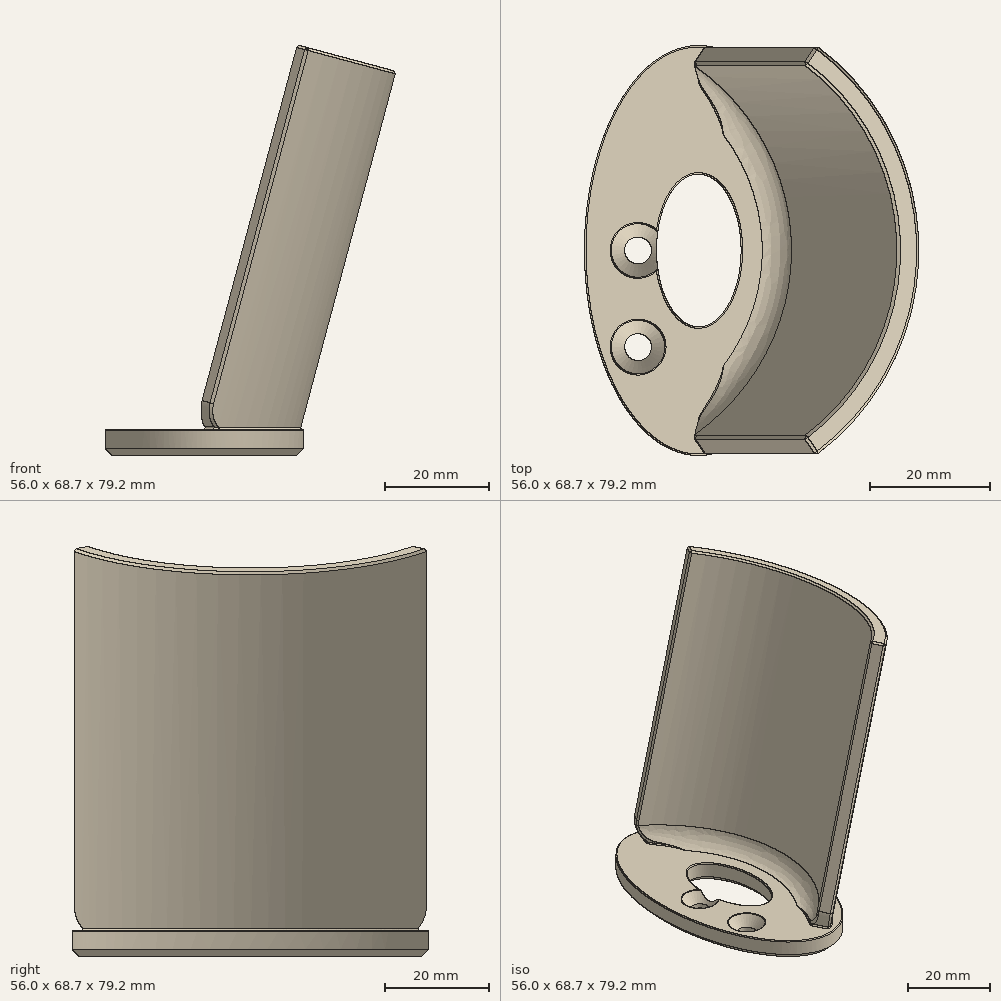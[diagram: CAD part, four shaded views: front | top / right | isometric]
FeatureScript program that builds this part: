
annotation { "Feature Type Name" : "Feature", "Feature Type Description" : "" }
export const myFeature = defineFeature(function(context is Context, id is Id, definition is map)
    precondition{}
    {
        {
            var Q0;
            Q0=qCreatedBy(makeId("Top.planeOp"),FACE);
            var sketch = newSketch(context, id + "F0", { "sketchPlane" : qUnion([Q0])});
            skLineSegment(sketch, "E0", {"start": v(0, -32.6) * mm, "end": v(0, 55.82) * mm, "construction": true});
            skSolve(sketch);
        }
        {
            var Q0;
            Q0=sQuery(id+"F0.wireOp",EDGE,"E0");
            cPlane(context, id + "F1", {"entities" : qUnion([Q0]), "cplaneType" : CPlaneType.LINE_ANGLE, "offset" : 25.4 * mm, "angle" : 15 * degree, "width" : 152.4 * mm, "height" : 152.4 * mm});
        }
        {
            var Q0;
            Q0=qCreatedBy(id+"F1.planeOp",FACE);
            var sketch = newSketch(context, id + "F2", { "sketchPlane" : qUnion([Q0])});
            skArc(sketch, "E1", {"start": v(21.85, -31.2) * mm, "mid": v(38.1, 0) * mm, "end": v(21.85, 31.2) * mm});
            skArc(sketch, "E2", {"start": v(24.04, -34.33) * mm, "mid": v(41.91, 0) * mm, "end": v(24.04, 34.33) * mm});
            skLineSegment(sketch, "E3", {"start": v(21.85, -31.2) * mm, "end": v(24.04, -34.33) * mm});
            skLineSegment(sketch, "E4", {"start": v(-21.31, 0) * mm, "end": v(0, 0) * mm, "construction": true});
            skLineSegment(sketch, "E5.MirrorCS", {"start": v(21.85, 31.2) * mm, "end": v(24.04, 34.33) * mm});
            skPoint(sketch, "E6.orphan", {"position": v(31.22, -44.6) * mm});
            skPoint(sketch, "E7.orphan", {"position": v(31.22, 44.6) * mm});
            skSolve(sketch);
        }
        {
            var Q0;
            Q0 = qSketchRegion(id + "F2", true);
            extrude(context, id + "F3", {"entities" : qUnion([Q0]), "depth" : 76.2 * mm});
        }
        {
            var Q0;
            Q0=qCreatedBy(makeId("Top.planeOp"),FACE);
            cPlane(context, id + "F4", {"entities" : qUnion([Q0]), "cplaneType" : CPlaneType.OFFSET, "offset" : 6.35 * mm, "oppositeDirection" : true, "width" : 152.4 * mm, "height" : 152.4 * mm});
        }
        {
            var Q0;
            Q0=qCreatedBy(id+"F4.planeOp",FACE);
            var sketch = newSketch(context, id + "F5", { "sketchPlane" : qUnion([Q0])});
            skLineSegment(sketch, "E8", {"start": v(23.22, 34.33) * mm, "end": v(23.22, -44.52) * mm, "construction": true});
            skEllipse(sketch, "E9", {"center": v(23.22, 0) * mm, "majorRadius": 34.33 * mm, "minorRadius": 19.16 * mm, "majorAxis": v(0, 1)});
            skSolve(sketch);
        }
        {
            var Q0;
            Q0 = qSketchRegion(id + "F5", true);
            extrude(context, id + "F6", {"entities" : qUnion([Q0]), "operationType" : NewBodyOperationType.ADD, "oppositeDirection" : true, "depth" : 5.08 * mm});
        }
        {
            var Q0;
            Q0=makeQuery(id+"F6.opExtrude","CAP_FACE",FACE,{"disambiguationData":[OSD([sQuery(id+"F5.wireOp",EDGE,"E9")])],"isStart":true});
            var sketch = newSketch(context, id + "F7", { "sketchPlane" : qUnion([Q0])});
            skEllipse(sketch, "E10", {"center": v(23.22, 0) * mm, "majorRadius": 12.78 * mm, "minorRadius": 7.1 * mm, "majorAxis": v(0, 1)});
            skSolve(sketch);
        }
        {
            var Q0;
            Q0 = qSketchRegion(id + "F7", true);
            extrude(context, id + "F8", {"entities" : qUnion([Q0]), "operationType" : NewBodyOperationType.REMOVE, "oppositeDirection" : true, "depth" : 25.4 * mm});
        }
        {
            var Q0;
            Q0=makeQuery(id+"F6.opExtrude","CAP_FACE",FACE,{"disambiguationData":[OSD([sQuery(id+"F5.wireOp",EDGE,"E9")])],"isStart":true});
            var sketch = newSketch(context, id + "F9", { "sketchPlane" : qUnion([Q0])});
            skLineSegment(sketch, "E11", {"start": v(13.06, -34.14) * mm, "end": v(13.06, 47.46) * mm, "construction": true});
            skPoint(sketch, "E12", {"position": v(13.06, -16.19) * mm});
            skLineSegment(sketch, "E13", {"start": v(23.22, 0) * mm, "end": v(23.22, -16.19) * mm, "construction": true});
            skPoint(sketch, "E14", {"position": v(13.06, 0) * mm});
            skSolve(sketch);
        }
        {
            var Q0;
            Q0=sQuery(id+"F9.wireOp",VERTEX,"E12");
            var Q1;
            Q1=makeQuery(id+"F3.opExtrude","SWEPT_BODY",BODY,{"disambiguationData":[OSD([sQuery(id+"F2.wireOp",EDGE,"E1"),sQuery(id+"F2.wireOp",EDGE,"E2"),sQuery(id+"F2.wireOp",EDGE,"E3"),sQuery(id+"F2.wireOp",EDGE,"E5.MirrorCS")])]});
            hole(context, id + "F10", {"style" : HoleStyle.C_SINK, "endStyle" : HoleEndStyle.BLIND, "standardTappedOrClearance" : lookupTablePath({ "standard" : "ANSI", "fit" : "Normal (ASME)", "size" : "#8", "type" : "Clearance" }), "standardBlindInLast" : lookupTablePath({ "fit" : "Free", "standard" : "ANSI", "size" : "#8", "type" : "Clearance" }), "holeDiameter" : 4.5 * mm, "cSinkDiameter" : 9.12 * mm, "cSinkAngle" : 82 * degree, "holeDepth" : 12.7 * mm, "isTappedThrough" : true, "tappedDepth" : 12.7 * mm, "tapClearance" : 3, "locations" : qUnion([Q0]), "scope" : qUnion([Q1])});
        }
        {
            var Q0;
            Q0=sQuery(id+"F9.wireOp",VERTEX,"E14");
            var Q1;
            Q1=makeQuery(id+"F3.opExtrude","SWEPT_BODY",BODY,{"disambiguationData":[OSD([sQuery(id+"F2.wireOp",EDGE,"E1"),sQuery(id+"F2.wireOp",EDGE,"E2"),sQuery(id+"F2.wireOp",EDGE,"E3"),sQuery(id+"F2.wireOp",EDGE,"E5.MirrorCS")])]});
            hole(context, id + "F11", {"style" : HoleStyle.C_SINK, "endStyle" : HoleEndStyle.BLIND, "standardTappedOrClearance" : lookupTablePath({ "standard" : "ANSI", "fit" : "Normal (ASME)", "size" : "#8", "type" : "Clearance" }), "standardBlindInLast" : lookupTablePath({ "fit" : "Free", "standard" : "ANSI", "size" : "#8", "type" : "Clearance" }), "holeDiameter" : 4.5 * mm, "cSinkDiameter" : 9.12 * mm, "cSinkAngle" : 82 * degree, "holeDepth" : 12.7 * mm, "isTappedThrough" : true, "tappedDepth" : 12.7 * mm, "tapClearance" : 3, "locations" : qUnion([Q0]), "scope" : qUnion([Q1])});
        }
        {
            var Q0;
            Q0=makeQuery(id+"F6.boolean.opBoolean","INTERSECT",EDGE,{"derivedFrom":[makeQuery(id+"F3.opExtrude","SWEPT_FACE",FACE,{"disambiguationData":[OSD([sQuery(id+"F2.wireOp",EDGE,"E1")])]}),makeQuery(id+"F6.opExtrude","CAP_FACE",FACE,{"disambiguationData":[OSD([sQuery(id+"F5.wireOp",EDGE,"E9")])],"isStart":true})]});
            fillet(context, id + "F12", {"entities" : qUnion([Q0]), "radius" : 5.08 * mm, "tangentPropagation" : true, "allowEdgeOverflow" : false});
        }
        {
            var Q0;
            Q0=makeQuery(id+"F3.opExtrude","CAP_EDGE",EDGE,{"disambiguationData":[OSD([sQuery(id+"F2.wireOp",EDGE,"E3")])],"isStart":true});
            var Q1;
            Q1=makeQuery(id+"F3.opExtrude","CAP_EDGE",EDGE,{"disambiguationData":[OSD([sQuery(id+"F2.wireOp",EDGE,"E5.MirrorCS")])],"isStart":true});
            fillet(context, id + "F13", {"entities" : qUnion([Q0, Q1]), "radius" : 5.08 * mm, "tangentPropagation" : true, "allowEdgeOverflow" : false});
        }
        {
            var Q0;
            Q0=makeQuery(id+"F6.opExtrude","CAP_FACE",FACE,{"disambiguationData":[OSD([sQuery(id+"F5.wireOp",EDGE,"E9")])],"isStart":false});
            chamfer(context, id + "F14", {"entities" : qUnion([Q0]), "width" : 1.27 * mm, "tangentPropagation" : true});
        }
        {
            var Q0;
            Q0=makeQuery(id+"F3.opExtrude","CAP_FACE",FACE,{"disambiguationData":[OSD([sQuery(id+"F2.wireOp",EDGE,"E1"),sQuery(id+"F2.wireOp",EDGE,"E2"),sQuery(id+"F2.wireOp",EDGE,"E3"),sQuery(id+"F2.wireOp",EDGE,"E5.MirrorCS")])],"isStart":false});
            var Q1;
            Q1=makeQuery(id+"F3.opExtrude","SWEPT_FACE",FACE,{"disambiguationData":[OSD([sQuery(id+"F2.wireOp",EDGE,"E3")])]});
            var Q2;
            Q2=makeQuery(id+"F3.opExtrude","SWEPT_FACE",FACE,{"disambiguationData":[OSD([sQuery(id+"F2.wireOp",EDGE,"E5.MirrorCS")])]});
            chamfer(context, id + "F15", {"entities" : qUnion([Q0, Q1, Q2]), "width" : 0.5 * mm, "tangentPropagation" : true});
        }
        {
            var Q0;
            Q0=makeQuery(id+"F6.opExtrude","CAP_FACE",FACE,{"disambiguationData":[OSD([sQuery(id+"F5.wireOp",EDGE,"E9")])],"isStart":true});
            fillet(context, id + "F16", {"entities" : qUnion([Q0]), "radius" : 0.25 * mm, "tangentPropagation" : true, "allowEdgeOverflow" : false});
        }
    });
